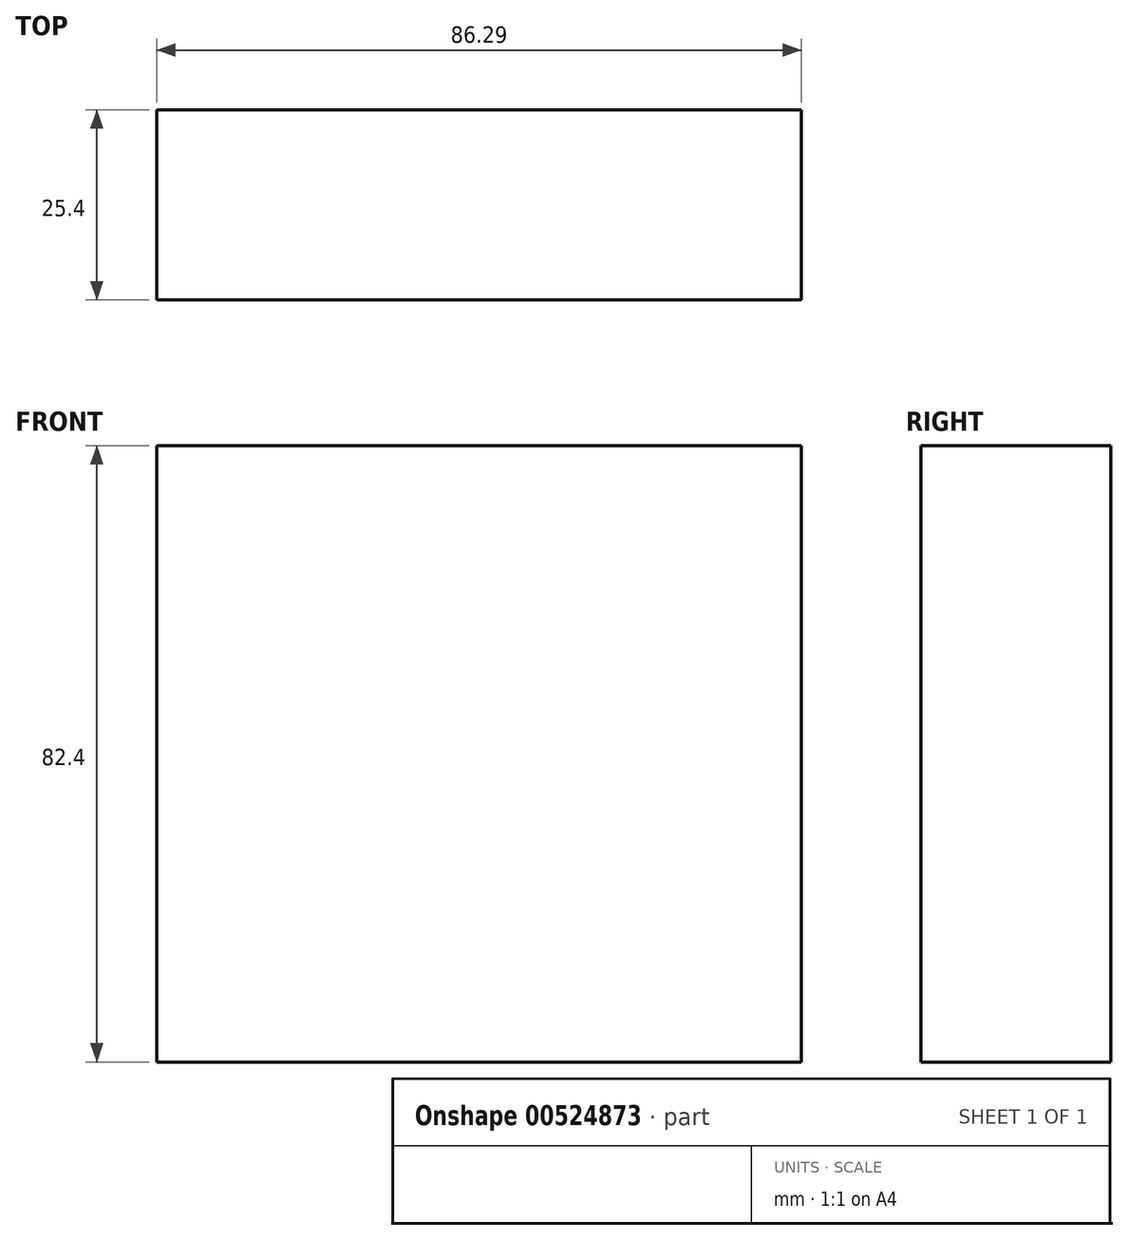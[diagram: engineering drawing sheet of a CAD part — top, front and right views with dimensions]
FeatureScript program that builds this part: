
annotation { "Feature Type Name" : "Feature", "Feature Type Description" : "" }
export const myFeature = defineFeature(function(context is Context, id is Id, definition is map)
    precondition{}
    {
        {
            var Q0;
            Q0=qCreatedBy(makeId("Front.planeOp"),FACE);
            var sketch = newSketch(context, id + "F0", { "sketchPlane" : qUnion([Q0])});
            skLineSegment(sketch, "E0.bottom", {"start": v(-44.97, 43.94) * mm, "end": v(41.32, 43.94) * mm});
            skLineSegment(sketch, "E0.top", {"start": v(-44.97, -38.46) * mm, "end": v(41.32, -38.46) * mm});
            skLineSegment(sketch, "E0.left", {"start": v(-44.97, 43.94) * mm, "end": v(-44.97, -38.46) * mm});
            skLineSegment(sketch, "E0.right", {"start": v(41.32, 43.94) * mm, "end": v(41.32, -38.46) * mm});
            skSolve(sketch);
        }
        {
            var Q0;
            Q0 = qSketchRegion(id + "F0", true);
            extrude(context, id + "F1", {"entities" : qUnion([Q0]), "depth" : 25.4 * mm, "offsetDistance" : 25.4 * mm});
        }
    });
